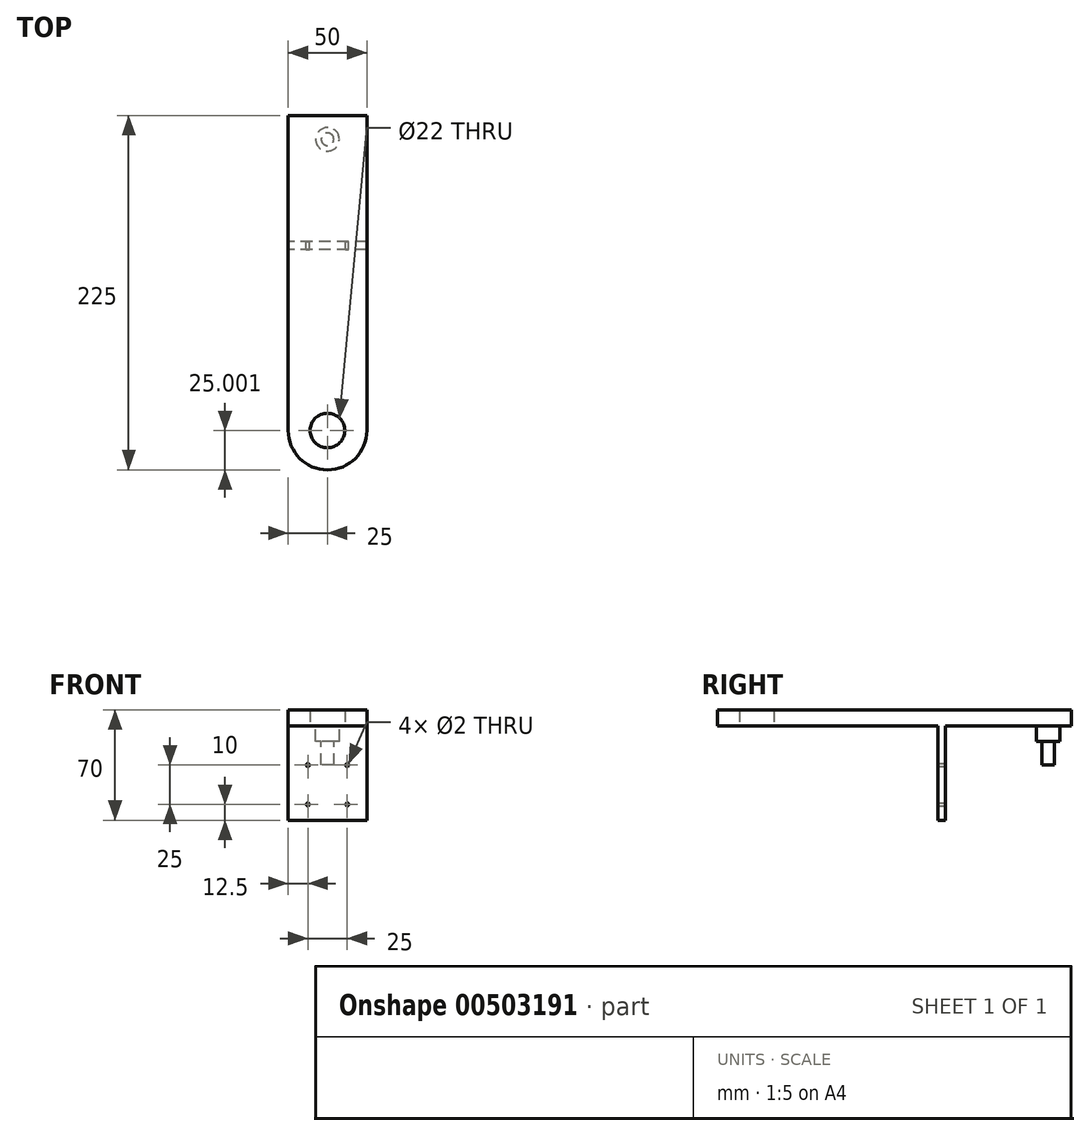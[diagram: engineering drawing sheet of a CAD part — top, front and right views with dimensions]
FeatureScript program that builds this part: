
annotation { "Feature Type Name" : "Feature", "Feature Type Description" : "" }
export const myFeature = defineFeature(function(context is Context, id is Id, definition is map)
    precondition{}
    {
        {
            var Q0;
            Q0=qCreatedBy(makeId("Top.planeOp"),FACE);
            var sketch = newSketch(context, id + "F0", { "sketchPlane" : qUnion([Q0])});
            skCircle(sketch, "E0", {"center": v(0, -92.19) * mm, "radius": 11 * mm});
            skArc(sketch, "E1", {"start": v(-25, -92.19) * mm, "mid": v(0, -117.19) * mm, "end": v(25, -92.19) * mm});
            skLineSegment(sketch, "E2", {"start": v(-25, -92.19) * mm, "end": v(-25, 107.81) * mm});
            skLineSegment(sketch, "E3", {"start": v(-25, 107.81) * mm, "end": v(25, 107.81) * mm});
            skLineSegment(sketch, "E4", {"start": v(25, 107.81) * mm, "end": v(25, -92.19) * mm});
            skLineSegment(sketch, "E5.bottom", {"start": v(25, 27.81) * mm, "end": v(-25, 27.81) * mm});
            skLineSegment(sketch, "E5.top", {"start": v(25, 22.81) * mm, "end": v(-25, 22.81) * mm});
            skLineSegment(sketch, "E5.left", {"start": v(25, 27.81) * mm, "end": v(25, 22.81) * mm});
            skLineSegment(sketch, "E5.right", {"start": v(-25, 27.81) * mm, "end": v(-25, 22.81) * mm});
            skCircle(sketch, "E6", {"center": v(0, 92.81) * mm, "radius": 7.5 * mm});
            skCircle(sketch, "E7", {"center": v(0, 92.81) * mm, "radius": 4 * mm});
            skSolve(sketch);
        }
        {
            var Q0;
            Q0=makeQuery(id+"F0.imprint","IMPRINT",FACE,{"disambiguationData":[TD([[makeQuery(id+"F0.imprint","IMPRINT",EDGE,{"derivedFrom":sQuery(id+"F0.wireOp",EDGE,"E0")}),-1.0]])]});
            var Q1;
            Q1=makeQuery(id+"F0.imprint","IMPRINT",FACE,{"disambiguationData":[TD([[makeQuery(id+"F0.imprint","IMPRINT",EDGE,{"derivedFrom":sQuery(id+"F0.wireOp",EDGE,"E5.bottom")}),1.0]])]});
            var Q2;
            {var subQ2=sQuery(id+"F0.wireOp",EDGE,"E3");Q2=makeQuery(id+"F0.imprint","IMPRINT",FACE,{"disambiguationData":[TD([[makeQuery(id+"F0.imprint","IMPRINT",EDGE,{"derivedFrom":subQ2}),-1.0]])]});}
            var Q3;
            Q3=makeQuery(id+"F0.imprint","IMPRINT",FACE,{"disambiguationData":[TD([[makeQuery(id+"F0.imprint","IMPRINT",EDGE,{"derivedFrom":sQuery(id+"F0.wireOp",EDGE,"E7")}),1.0]])]});
            var Q4;
            Q4=makeQuery(id+"F0.imprint","IMPRINT",FACE,{"disambiguationData":[TD([[makeQuery(id+"F0.imprint","IMPRINT",EDGE,{"derivedFrom":sQuery(id+"F0.wireOp",EDGE,"E6")}),1.0]])]});
            var Q5;
            Q5=sQuery(id+"F0.wireOp",EDGE,"E0");
            var Q6;
            Q6=sQuery(id+"F0.wireOp",EDGE,"E1");
            var Q7;
            Q7=sQuery(id+"F0.wireOp",EDGE,"E2");
            var Q8;
            Q8=sQuery(id+"F0.wireOp",EDGE,"E3");
            var Q9;
            Q9=sQuery(id+"F0.wireOp",EDGE,"E4");
            var Q10;
            Q10=sQuery(id+"F0.wireOp",EDGE,"E5.bottom");
            var Q11;
            Q11=sQuery(id+"F0.wireOp",EDGE,"E5.top");
            var Q12;
            Q12=sQuery(id+"F0.wireOp",EDGE,"E5.left");
            var Q13;
            Q13=sQuery(id+"F0.wireOp",EDGE,"E5.right");
            var Q14;
            Q14=sQuery(id+"F0.wireOp",EDGE,"E6");
            var Q15;
            Q15=sQuery(id+"F0.wireOp",EDGE,"E7");
            extrude(context, id + "F1", {"entities" : qUnion([Q0, Q1, Q2, Q3, Q4]), "surfaceEntities" : qUnion([Q5, Q6, Q7, Q8, Q9, Q10, Q11, Q12, Q13, Q14, Q15]), "depth" : 10 * mm});
        }
        {
            var Q0;
            Q0=makeQuery(id+"F0.imprint","IMPRINT",FACE,{"disambiguationData":[TD([[makeQuery(id+"F0.imprint","IMPRINT",EDGE,{"derivedFrom":sQuery(id+"F0.wireOp",EDGE,"E5.bottom")}),1.0]])]});
            extrude(context, id + "F2", {"entities" : qUnion([Q0]), "operationType" : NewBodyOperationType.ADD, "oppositeDirection" : true, "depth" : 60 * mm});
        }
        {
            var Q0;
            Q0=makeQuery(id+"F0.imprint","IMPRINT",FACE,{"disambiguationData":[TD([[makeQuery(id+"F0.imprint","IMPRINT",EDGE,{"derivedFrom":sQuery(id+"F0.wireOp",EDGE,"E6")}),1.0]])]});
            extrude(context, id + "F3", {"entities" : qUnion([Q0]), "operationType" : NewBodyOperationType.ADD, "oppositeDirection" : true, "depth" : 10 * mm});
        }
        {
            var Q0;
            Q0=makeQuery(id+"F0.imprint","IMPRINT",FACE,{"disambiguationData":[TD([[makeQuery(id+"F0.imprint","IMPRINT",EDGE,{"derivedFrom":sQuery(id+"F0.wireOp",EDGE,"E7")}),1.0]])]});
            extrude(context, id + "F4", {"entities" : qUnion([Q0]), "operationType" : NewBodyOperationType.ADD, "oppositeDirection" : true, "depth" : 25 * mm});
        }
        {
            var Q0;
            Q0=makeQuery(id+"F2.opExtrude","SWEPT_FACE",FACE,{"disambiguationData":[OSD([sQuery(id+"F0.wireOp",EDGE,"E5.bottom")])]});
            var sketch = newSketch(context, id + "F5", { "sketchPlane" : qUnion([Q0])});
            skLineSegment(sketch, "E8.bottom", {"start": v(-12.5, -25) * mm, "end": v(12.5, -25) * mm, "construction": true});
            skLineSegment(sketch, "E8.top", {"start": v(-12.5, -50) * mm, "end": v(12.5, -50) * mm, "construction": true});
            skLineSegment(sketch, "E8.left", {"start": v(-12.5, -25) * mm, "end": v(-12.5, -50) * mm, "construction": true});
            skLineSegment(sketch, "E8.right", {"start": v(12.5, -25) * mm, "end": v(12.5, -50) * mm, "construction": true});
            skCircle(sketch, "E9", {"center": v(-12.5, -50) * mm, "radius": 1 * mm});
            skCircle(sketch, "E10", {"center": v(-12.5, -25) * mm, "radius": 1 * mm});
            skCircle(sketch, "E11", {"center": v(12.5, -25) * mm, "radius": 1 * mm});
            skCircle(sketch, "E12", {"center": v(12.5, -50) * mm, "radius": 1 * mm});
            skSolve(sketch);
        }
        {
            var Q0;
            Q0=makeQuery(id+"F5.imprint","IMPRINT",FACE,{"disambiguationData":[TD([[makeQuery(id+"F5.imprint","IMPRINT",EDGE,{"derivedFrom":sQuery(id+"F5.wireOp",EDGE,"E10")}),1.0]])]});
            var Q1;
            Q1=makeQuery(id+"F5.imprint","IMPRINT",FACE,{"disambiguationData":[TD([[makeQuery(id+"F5.imprint","IMPRINT",EDGE,{"derivedFrom":sQuery(id+"F5.wireOp",EDGE,"E11")}),1.0]])]});
            var Q2;
            Q2=makeQuery(id+"F5.imprint","IMPRINT",FACE,{"disambiguationData":[TD([[makeQuery(id+"F5.imprint","IMPRINT",EDGE,{"derivedFrom":sQuery(id+"F5.wireOp",EDGE,"E9")}),1.0]])]});
            var Q3;
            Q3=makeQuery(id+"F5.imprint","IMPRINT",FACE,{"disambiguationData":[TD([[makeQuery(id+"F5.imprint","IMPRINT",EDGE,{"derivedFrom":sQuery(id+"F5.wireOp",EDGE,"E12")}),1.0]])]});
            extrude(context, id + "F6", {"entities" : qUnion([Q0, Q1, Q2, Q3]), "operationType" : NewBodyOperationType.REMOVE, "oppositeDirection" : true, "depth" : 25 * mm});
        }
    });
